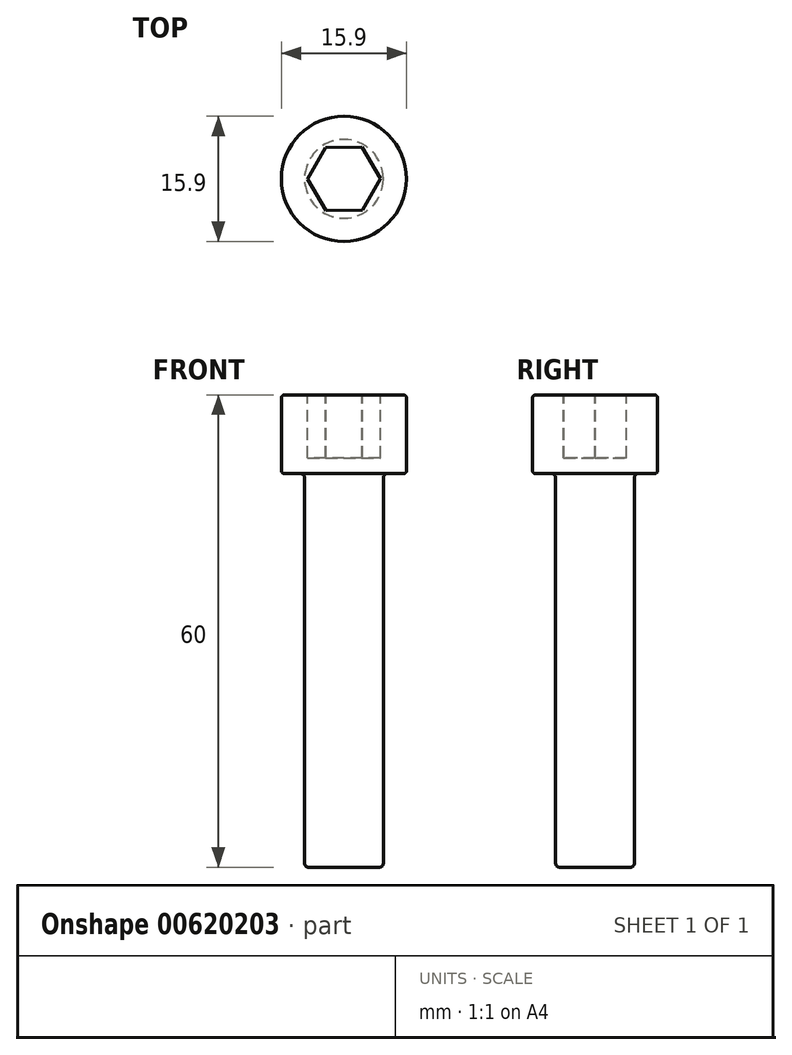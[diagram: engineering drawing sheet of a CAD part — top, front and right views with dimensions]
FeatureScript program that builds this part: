
annotation { "Feature Type Name" : "Feature", "Feature Type Description" : "" }
export const myFeature = defineFeature(function(context is Context, id is Id, definition is map)
    precondition{}
    {
        {
            var Q0;
            Q0=qCreatedBy(makeId("Right.planeOp"),FACE);
            var sketch = newSketch(context, id + "F0", { "sketchPlane" : qUnion([Q0])});
            skLineSegment(sketch, "E0", {"start": v(0, 0) * mm, "end": v(0, -60) * mm, "construction": true});
            skLineSegment(sketch, "E1", {"start": v(0, 0) * mm, "end": v(-7.95, 0) * mm});
            skLineSegment(sketch, "E2", {"start": v(-7.95, 0) * mm, "end": v(-7.95, -10) * mm});
            skLineSegment(sketch, "E3", {"start": v(-7.95, -10) * mm, "end": v(-5, -10) * mm});
            skLineSegment(sketch, "E4", {"start": v(-5, -10) * mm, "end": v(-5, -60) * mm});
            skLineSegment(sketch, "E5", {"start": v(-5, -60) * mm, "end": v(0, -60) * mm});
            skLineSegment(sketch, "E6", {"start": v(0, 0) * mm, "end": v(0, -60) * mm});
            skSolve(sketch);
        }
        {
            var Q0;
            Q0=makeQuery(id+"F0.imprint","IMPRINT",FACE,{"disambiguationData":[TD([[makeQuery(id+"F0.imprint","IMPRINT",EDGE,{"derivedFrom":sQuery(id+"F0.wireOp",EDGE,"E1")}),1.0]])]});
            var Q1;
            Q1=sQuery(id+"F0.wireOp",EDGE,"E6");
            revolve(context, id + "F1", {"entities" : qUnion([Q0]), "axis" : qUnion([Q1]), "revolveType" : RevolveType.FULL});
        }
        {
            var Q0;
            Q0=makeQuery(id+"F1.opRevolve","SWEPT_FACE",FACE,{"disambiguationData":[OSD([sQuery(id+"F0.wireOp",EDGE,"E1")])]});
            var sketch = newSketch(context, id + "F2", { "sketchPlane" : qUnion([Q0])});
            skCircle(sketch, "E7.cCircle", {"center": v(0, 0) * mm, "radius": 4 * mm, "construction": true});
            skLineSegment(sketch, "E7.0", {"start": v(-4.62, -0.04) * mm, "end": v(-2.34, 3.98) * mm});
            skLineSegment(sketch, "E7.1", {"start": v(-2.34, 3.98) * mm, "end": v(2.28, 4.02) * mm});
            skLineSegment(sketch, "E7.2", {"start": v(2.28, 4.02) * mm, "end": v(4.62, 0.04) * mm});
            skLineSegment(sketch, "E7.3", {"start": v(4.62, 0.04) * mm, "end": v(2.34, -3.98) * mm});
            skLineSegment(sketch, "E7.4", {"start": v(2.34, -3.98) * mm, "end": v(-2.28, -4.02) * mm});
            skLineSegment(sketch, "E7.5", {"start": v(-2.28, -4.02) * mm, "end": v(-4.62, -0.04) * mm});
            skPoint(sketch, "E7.0.midPoint", {"position": v(-3.48, 1.97) * mm});
            skSolve(sketch);
        }
        {
            var Q0;
            Q0=makeQuery(id+"F2.imprint","IMPRINT",FACE,{"disambiguationData":[TD([[makeQuery(id+"F2.imprint","IMPRINT",EDGE,{"derivedFrom":sQuery(id+"F2.wireOp",EDGE,"E7.0")}),-1.0]])]});
            extrude(context, id + "F3", {"entities" : qUnion([Q0]), "operationType" : NewBodyOperationType.REMOVE, "oppositeDirection" : true, "depth" : 8 * mm, "offsetDistance" : 25 * mm});
        }
        {
            var Q0;
            Q0=makeQuery(id+"F1.opRevolve","SWEPT_EDGE",EDGE,{"disambiguationData":[OSD([sQuery(id+"F0.wireOp",EDGE,"E1"),sQuery(id+"F0.wireOp",EDGE,"E2")])]});
            var Q1;
            Q1=makeQuery(id+"F1.opRevolve","SWEPT_EDGE",EDGE,{"disambiguationData":[OSD([sQuery(id+"F0.wireOp",EDGE,"E2"),sQuery(id+"F0.wireOp",EDGE,"E3")])]});
            fillet(context, id + "F4", {"entities" : qUnion([Q0, Q1]), "radius" : 0.4 * mm, "tangentPropagation" : true, "allowEdgeOverflow" : false});
        }
        {
            var Q0;
            Q0=makeQuery(id+"F1.opRevolve","SWEPT_EDGE",EDGE,{"disambiguationData":[OSD([sQuery(id+"F0.wireOp",EDGE,"E3"),sQuery(id+"F0.wireOp",EDGE,"E4")])]});
            var Q1;
            Q1=makeQuery(id+"F1.opRevolve","SWEPT_EDGE",EDGE,{"disambiguationData":[OSD([sQuery(id+"F0.wireOp",EDGE,"E4"),sQuery(id+"F0.wireOp",EDGE,"E5")])]});
            fillet(context, id + "F5", {"entities" : qUnion([Q0, Q1]), "radius" : 0.5 * mm, "tangentPropagation" : true, "allowEdgeOverflow" : false});
        }
    });
